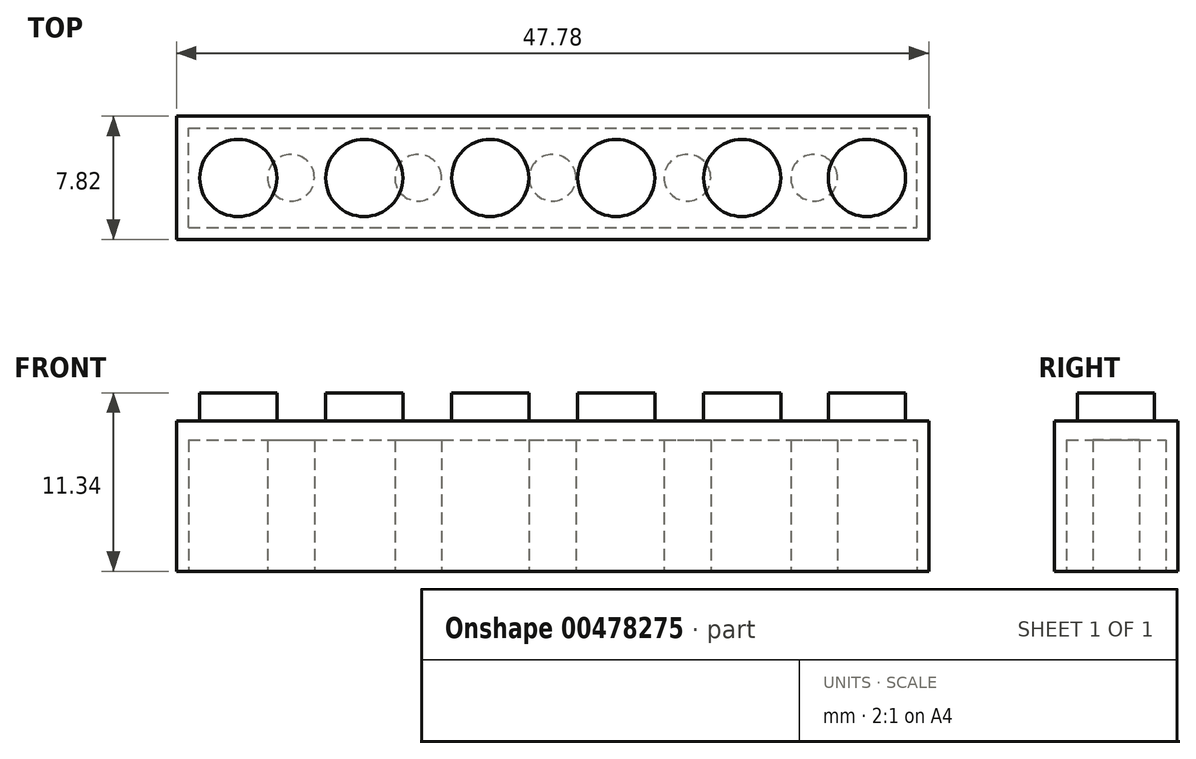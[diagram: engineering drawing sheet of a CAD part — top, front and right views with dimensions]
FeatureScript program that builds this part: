
annotation { "Feature Type Name" : "Feature", "Feature Type Description" : "" }
export const myFeature = defineFeature(function(context is Context, id is Id, definition is map)
    precondition{}
    {
        {
            var Q0;
            Q0=qCreatedBy(makeId("Top.planeOp"),FACE);
            var sketch = newSketch(context, id + "F0", { "sketchPlane" : qUnion([Q0])});
            skLineSegment(sketch, "E0.bottom", {"start": v(-23.89, 3.91) * mm, "end": v(23.89, 3.91) * mm});
            skLineSegment(sketch, "E0.top", {"start": v(-23.89, -3.91) * mm, "end": v(23.89, -3.91) * mm});
            skLineSegment(sketch, "E0.left", {"start": v(-23.89, 3.91) * mm, "end": v(-23.89, -3.91) * mm});
            skLineSegment(sketch, "E0.right", {"start": v(23.89, 3.91) * mm, "end": v(23.89, -3.91) * mm});
            skPoint(sketch, "E0.middle", {"position": v(0, 0) * mm});
            skSolve(sketch);
        }
        {
            var Q0;
            Q0=makeQuery(id+"F0.imprint","IMPRINT",FACE,{"disambiguationData":[TD([[makeQuery(id+"F0.imprint","IMPRINT",EDGE,{"derivedFrom":sQuery(id+"F0.wireOp",EDGE,"E0.bottom")}),-1.0]])]});
            extrude(context, id + "F1", {"entities" : qUnion([Q0]), "endBound" : BoundingType.SYMMETRIC, "depth" : 9.56 * mm});
        }
        {
            var Q0;
            Q0=makeQuery(id+"F1.opExtrude","CAP_FACE",FACE,{"disambiguationData":[OSD([sQuery(id+"F0.wireOp",EDGE,"E0.bottom"),sQuery(id+"F0.wireOp",EDGE,"E0.top"),sQuery(id+"F0.wireOp",EDGE,"E0.left"),sQuery(id+"F0.wireOp",EDGE,"E0.right")])],"isStart":false});
            var sketch = newSketch(context, id + "F2", { "sketchPlane" : qUnion([Q0])});
            skCircle(sketch, "E1", {"center": v(-19.96, -0.01) * mm, "radius": 2.45 * mm});
            skSolve(sketch);
        }
        {
            var Q0;
            Q0=makeQuery(id+"F2.imprint","IMPRINT",FACE,{"disambiguationData":[TD([[makeQuery(id+"F2.imprint","IMPRINT",EDGE,{"derivedFrom":sQuery(id+"F2.wireOp",EDGE,"E1")}),-1.0]])]});
            var sketch = newSketch(context, id + "F3", { "sketchPlane" : qUnion([Q0])});
            skCircle(sketch, "E2", {"center": v(-11.96, -0.01) * mm, "radius": 2.45 * mm});
            skSolve(sketch);
        }
        {
            var Q0;
            Q0=makeQuery(id+"F2.imprint","IMPRINT",FACE,{"disambiguationData":[TD([[makeQuery(id+"F2.imprint","IMPRINT",EDGE,{"derivedFrom":sQuery(id+"F2.wireOp",EDGE,"E1")}),-1.0]])]});
            var sketch = newSketch(context, id + "F4", { "sketchPlane" : qUnion([Q0])});
            skCircle(sketch, "E3", {"center": v(-3.96, -0.01) * mm, "radius": 2.45 * mm});
            skSolve(sketch);
        }
        {
            var Q0;
            Q0=makeQuery(id+"F2.imprint","IMPRINT",FACE,{"disambiguationData":[TD([[makeQuery(id+"F2.imprint","IMPRINT",EDGE,{"derivedFrom":sQuery(id+"F2.wireOp",EDGE,"E1")}),-1.0]])]});
            var sketch = newSketch(context, id + "F5", { "sketchPlane" : qUnion([Q0])});
            skCircle(sketch, "E4", {"center": v(4.04, -0.01) * mm, "radius": 2.45 * mm});
            skSolve(sketch);
        }
        {
            var Q0;
            Q0=makeQuery(id+"F2.imprint","IMPRINT",FACE,{"disambiguationData":[TD([[makeQuery(id+"F2.imprint","IMPRINT",EDGE,{"derivedFrom":sQuery(id+"F2.wireOp",EDGE,"E1")}),-1.0]])]});
            var sketch = newSketch(context, id + "F6", { "sketchPlane" : qUnion([Q0])});
            skCircle(sketch, "E5", {"center": v(12.04, -0.01) * mm, "radius": 2.45 * mm});
            skSolve(sketch);
        }
        {
            var Q0;
            Q0=makeQuery(id+"F2.imprint","IMPRINT",FACE,{"disambiguationData":[TD([[makeQuery(id+"F2.imprint","IMPRINT",EDGE,{"derivedFrom":sQuery(id+"F2.wireOp",EDGE,"E1")}),-1.0]])]});
            var sketch = newSketch(context, id + "F7", { "sketchPlane" : qUnion([Q0])});
            skCircle(sketch, "E6", {"center": v(19.96, -0.01) * mm, "radius": 2.45 * mm});
            skSolve(sketch);
        }
        {
            var Q0;
            Q0=makeQuery(id+"F2.imprint","IMPRINT",FACE,{"disambiguationData":[TD([[makeQuery(id+"F2.imprint","IMPRINT",EDGE,{"derivedFrom":sQuery(id+"F2.wireOp",EDGE,"E1")}),1.0]])]});
            extrude(context, id + "F8", {"entities" : qUnion([Q0]), "operationType" : NewBodyOperationType.ADD, "depth" : 1.78 * mm});
        }
        {
            var Q0;
            Q0=makeQuery(id+"F3.imprint","IMPRINT",FACE,{"disambiguationData":[TD([[makeQuery(id+"F3.imprint","IMPRINT",EDGE,{"derivedFrom":sQuery(id+"F3.wireOp",EDGE,"E2")}),1.0]])]});
            extrude(context, id + "F9", {"entities" : qUnion([Q0]), "operationType" : NewBodyOperationType.ADD, "depth" : 1.78 * mm});
        }
        {
            var Q0;
            Q0=makeQuery(id+"F4.imprint","IMPRINT",FACE,{"disambiguationData":[TD([[makeQuery(id+"F4.imprint","IMPRINT",EDGE,{"derivedFrom":sQuery(id+"F4.wireOp",EDGE,"E3")}),1.0]])]});
            extrude(context, id + "F10", {"entities" : qUnion([Q0]), "operationType" : NewBodyOperationType.ADD, "depth" : 1.78 * mm});
        }
        {
            var Q0;
            Q0=makeQuery(id+"F5.imprint","IMPRINT",FACE,{"disambiguationData":[TD([[makeQuery(id+"F5.imprint","IMPRINT",EDGE,{"derivedFrom":sQuery(id+"F5.wireOp",EDGE,"E4")}),1.0]])]});
            extrude(context, id + "F11", {"entities" : qUnion([Q0]), "operationType" : NewBodyOperationType.ADD, "depth" : 1.78 * mm});
        }
        {
            var Q0;
            Q0=makeQuery(id+"F6.imprint","IMPRINT",FACE,{"disambiguationData":[TD([[makeQuery(id+"F6.imprint","IMPRINT",EDGE,{"derivedFrom":sQuery(id+"F6.wireOp",EDGE,"E5")}),1.0]])]});
            extrude(context, id + "F12", {"entities" : qUnion([Q0]), "operationType" : NewBodyOperationType.ADD, "depth" : 1.78 * mm});
        }
        {
            var Q0;
            Q0=makeQuery(id+"F7.imprint","IMPRINT",FACE,{"disambiguationData":[TD([[makeQuery(id+"F7.imprint","IMPRINT",EDGE,{"derivedFrom":sQuery(id+"F7.wireOp",EDGE,"E6")}),1.0]])]});
            extrude(context, id + "F13", {"entities" : qUnion([Q0]), "operationType" : NewBodyOperationType.ADD, "depth" : 1.78 * mm});
        }
        {
            var Q0;
            Q0=makeQuery(id+"F1.opExtrude","CAP_FACE",FACE,{"disambiguationData":[OSD([sQuery(id+"F0.wireOp",EDGE,"E0.bottom"),sQuery(id+"F0.wireOp",EDGE,"E0.top"),sQuery(id+"F0.wireOp",EDGE,"E0.left"),sQuery(id+"F0.wireOp",EDGE,"E0.right")])],"isStart":true});
            var sketch = newSketch(context, id + "F14", { "sketchPlane" : qUnion([Q0])});
            skLineSegment(sketch, "E7.bottom", {"start": v(-23.13, 3.15) * mm, "end": v(23.13, 3.15) * mm});
            skLineSegment(sketch, "E7.top", {"start": v(-23.13, -3.15) * mm, "end": v(23.13, -3.15) * mm});
            skLineSegment(sketch, "E7.left", {"start": v(-23.13, 3.15) * mm, "end": v(-23.13, -3.15) * mm});
            skLineSegment(sketch, "E7.right", {"start": v(23.13, 3.15) * mm, "end": v(23.13, -3.15) * mm});
            skPoint(sketch, "E7.middle", {"position": v(0, 0) * mm});
            skSolve(sketch);
        }
        {
            var Q0;
            Q0=makeQuery(id+"F14.imprint","IMPRINT",FACE,{"disambiguationData":[TD([[makeQuery(id+"F14.imprint","IMPRINT",EDGE,{"derivedFrom":sQuery(id+"F14.wireOp",EDGE,"E7.bottom")}),-1.0]])]});
            var sketch = newSketch(context, id + "F15", { "sketchPlane" : qUnion([Q0])});
            skCircle(sketch, "E8", {"center": v(-16.61, 0) * mm, "radius": 1.49 * mm});
            skSolve(sketch);
        }
        {
            var Q0;
            Q0=makeQuery(id+"F14.imprint","IMPRINT",FACE,{"disambiguationData":[TD([[makeQuery(id+"F14.imprint","IMPRINT",EDGE,{"derivedFrom":sQuery(id+"F14.wireOp",EDGE,"E7.bottom")}),-1.0]])]});
            var sketch = newSketch(context, id + "F16", { "sketchPlane" : qUnion([Q0])});
            skCircle(sketch, "E9", {"center": v(-8.53, 0) * mm, "radius": 1.49 * mm});
            skSolve(sketch);
        }
        {
            var Q0;
            Q0=makeQuery(id+"F14.imprint","IMPRINT",FACE,{"disambiguationData":[TD([[makeQuery(id+"F14.imprint","IMPRINT",EDGE,{"derivedFrom":sQuery(id+"F14.wireOp",EDGE,"E7.bottom")}),-1.0]])]});
            var sketch = newSketch(context, id + "F17", { "sketchPlane" : qUnion([Q0])});
            skCircle(sketch, "E10", {"center": v(0, 0) * mm, "radius": 1.49 * mm});
            skSolve(sketch);
        }
        {
            var Q0;
            Q0=makeQuery(id+"F14.imprint","IMPRINT",FACE,{"disambiguationData":[TD([[makeQuery(id+"F14.imprint","IMPRINT",EDGE,{"derivedFrom":sQuery(id+"F14.wireOp",EDGE,"E7.bottom")}),-1.0]])]});
            var sketch = newSketch(context, id + "F18", { "sketchPlane" : qUnion([Q0])});
            skCircle(sketch, "E11", {"center": v(16.61, 0) * mm, "radius": 1.49 * mm});
            skSolve(sketch);
        }
        {
            var Q0;
            Q0=makeQuery(id+"F14.imprint","IMPRINT",FACE,{"disambiguationData":[TD([[makeQuery(id+"F14.imprint","IMPRINT",EDGE,{"derivedFrom":sQuery(id+"F14.wireOp",EDGE,"E7.bottom")}),-1.0]])]});
            var sketch = newSketch(context, id + "F19", { "sketchPlane" : qUnion([Q0])});
            skCircle(sketch, "E12", {"center": v(8.56, 0) * mm, "radius": 1.49 * mm});
            skSolve(sketch);
        }
        {
            var Q0;
            Q0=makeQuery(id+"F14.imprint","IMPRINT",FACE,{"disambiguationData":[TD([[makeQuery(id+"F14.imprint","IMPRINT",EDGE,{"derivedFrom":sQuery(id+"F14.wireOp",EDGE,"E7.bottom")}),-1.0]])]});
            extrude(context, id + "F20", {"entities" : qUnion([Q0]), "operationType" : NewBodyOperationType.REMOVE, "oppositeDirection" : true, "depth" : 8.33 * mm, "offsetDistance" : 25.4 * mm});
        }
        {
            var Q0;
            Q0=makeQuery(id+"F15.imprint","IMPRINT",FACE,{"disambiguationData":[TD([[makeQuery(id+"F15.imprint","IMPRINT",EDGE,{"derivedFrom":sQuery(id+"F15.wireOp",EDGE,"E8")}),1.0]])]});
            extrude(context, id + "F21", {"entities" : qUnion([Q0]), "operationType" : NewBodyOperationType.ADD, "oppositeDirection" : true, "depth" : 8.33 * mm, "offsetDistance" : 25.4 * mm});
        }
        {
            var Q0;
            Q0=makeQuery(id+"F16.imprint","IMPRINT",FACE,{"disambiguationData":[TD([[makeQuery(id+"F16.imprint","IMPRINT",EDGE,{"derivedFrom":sQuery(id+"F16.wireOp",EDGE,"E9")}),1.0]])]});
            var Q1;
            Q1=sQuery(id+"F16.wireOp",EDGE,"E9");
            extrude(context, id + "F22", {"entities" : qUnion([Q0]), "operationType" : NewBodyOperationType.ADD, "surfaceEntities" : qUnion([Q1]), "oppositeDirection" : true, "depth" : 8.33 * mm, "offsetDistance" : 25.4 * mm});
        }
        {
            var Q0;
            Q0 = qSketchRegion(id + "F17", true);
            extrude(context, id + "F23", {"entities" : qUnion([Q0]), "operationType" : NewBodyOperationType.ADD, "oppositeDirection" : true, "depth" : 8.33 * mm, "offsetDistance" : 25.4 * mm});
        }
        {
            var Q0;
            Q0 = qSketchRegion(id + "F19", true);
            extrude(context, id + "F24", {"entities" : qUnion([Q0]), "operationType" : NewBodyOperationType.ADD, "oppositeDirection" : true, "depth" : 8.33 * mm, "offsetDistance" : 25.4 * mm});
        }
        {
            var Q0;
            Q0 = qSketchRegion(id + "F18", true);
            extrude(context, id + "F25", {"entities" : qUnion([Q0]), "operationType" : NewBodyOperationType.ADD, "oppositeDirection" : true, "depth" : 8.33 * mm, "offsetDistance" : 25.4 * mm});
        }
    });
